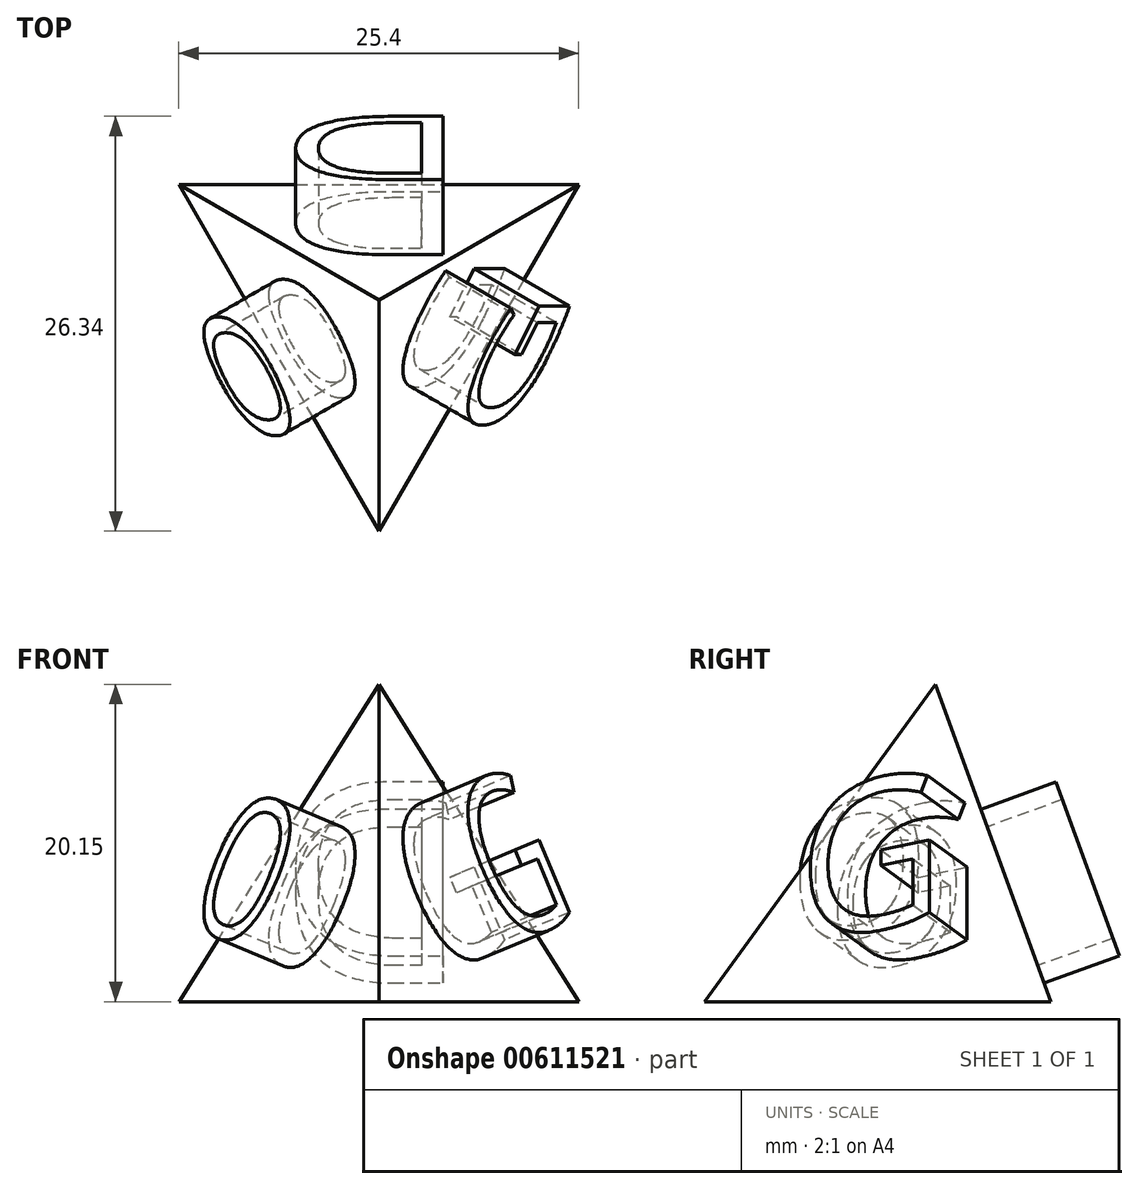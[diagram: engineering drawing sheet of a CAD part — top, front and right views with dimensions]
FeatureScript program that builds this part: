
annotation { "Feature Type Name" : "Feature", "Feature Type Description" : "" }
export const myFeature = defineFeature(function(context is Context, id is Id, definition is map)
    precondition{}
    {
        {
            var Q0;
            Q0=qCreatedBy(makeId("Top.planeOp"),FACE);
            var sketch = newSketch(context, id + "F0", { "sketchPlane" : qUnion([Q0])});
            skCircle(sketch, "E0.cCircle", {"center": v(0.35, 0) * mm, "radius": 7.33 * mm, "construction": true});
            skLineSegment(sketch, "E0.0", {"start": v(-12.35, 7.33) * mm, "end": v(13.05, 7.33) * mm});
            skLineSegment(sketch, "E0.1", {"start": v(13.05, 7.33) * mm, "end": v(0.35, -14.66) * mm});
            skLineSegment(sketch, "E0.2", {"start": v(0.35, -14.66) * mm, "end": v(-12.35, 7.33) * mm});
            skPoint(sketch, "E0.0.midPoint", {"position": v(0.35, 7.33) * mm});
            skSolve(sketch);
        }
        {
            var Q0;
            Q0 = qSketchRegion(id + "F0", true);
            extrude(context, id + "F1", {"entities" : qUnion([Q0]), "depth" : 25.4 * mm, "offsetDistance" : 25.4 * mm, "hasDraft" : true, "draftAngle" : 20 * degree, "draftPullDirection" : true});
        }
        {
            var Q0;
            Q0=makeQuery(id+"F1.opExtrude","SWEPT_FACE",FACE,{"disambiguationData":[OSD([sQuery(id+"F0.wireOp",EDGE,"E0.0")])]});
            var sketch = newSketch(context, id + "F2", { "sketchPlane" : qUnion([Q0])});
            skText(sketch, "E1", { "text": "D", "fontName": "OpenSans-Regular.ttf"});
            const initialGuessF2  = {"E1": [-0.00606, -0.00125, 1, 0, 0.01184]};
            skSetInitialGuess(sketch, initialGuessF2);
            skSolve(sketch);
        }
        {
            var Q0;
            Q0 = qSketchRegion(id + "F2", true);
            extrude(context, id + "F3", {"entities" : qUnion([Q0]), "operationType" : NewBodyOperationType.ADD, "depth" : 5.08 * mm, "offsetDistance" : 25.4 * mm});
        }
        {
            var Q0;
            Q0=makeQuery(id+"F1.opExtrude","SWEPT_FACE",FACE,{"disambiguationData":[OSD([sQuery(id+"F0.wireOp",EDGE,"E0.2")])]});
            var sketch = newSketch(context, id + "F4", { "sketchPlane" : qUnion([Q0])});
            skText(sketch, "E2", { "text": "O", "fontName": "OpenSans-Regular.ttf"});
            const initialGuessF4  = {"E2": [-0.00581, 0, 1, 0, 0.00938]};
            skSetInitialGuess(sketch, initialGuessF4);
            skSolve(sketch);
        }
        {
            var Q0;
            Q0 = qSketchRegion(id + "F4", true);
            extrude(context, id + "F5", {"entities" : qUnion([Q0]), "operationType" : NewBodyOperationType.ADD, "depth" : 5.08 * mm, "offsetDistance" : 25.4 * mm});
        }
        {
            var Q0;
            Q0=makeQuery(id+"F1.opExtrude","SWEPT_FACE",FACE,{"disambiguationData":[OSD([sQuery(id+"F0.wireOp",EDGE,"E0.1")])]});
            var sketch = newSketch(context, id + "F6", { "sketchPlane" : qUnion([Q0])});
            skText(sketch, "E3", { "text": "G", "fontName": "OpenSans-Regular.ttf"});
            const initialGuessF6  = {"E3": [-0.00336, 0, 1, 0, 0.0104]};
            skSetInitialGuess(sketch, initialGuessF6);
            skSolve(sketch);
        }
        {
            var Q0;
            Q0 = qSketchRegion(id + "F6", true);
            extrude(context, id + "F7", {"entities" : qUnion([Q0]), "operationType" : NewBodyOperationType.ADD, "depth" : 5.08 * mm, "offsetDistance" : 25.4 * mm});
        }
    });
